# Revit family: Tyco_Fireclass_Mid Tier-I_Control and Indicating Panels - FC500______
name_source: partatom
category: Generic Models
revit_build: Autodesk Revit 2016 (Build: 20150714_1515(x64)
units: mm (PartAtom-declared; Revit-internal decimal feet)

## family parameters
Always vertical = Yes
Can host rebar = No
Cut with Voids When Loaded = No
Host = Wall
Part Type = Normal
Room Calculation Point = No
Round Connector Dimension = Use Diameter
Shared = No

## types (1)
- FC500
    Asset Type = Moveable
    Brand = FireClass
    Colour = RAL 7035
    Description = Repeater for use with FC501, FC503 and FC506 panels
    Duration Unit = Year
    Finish = Fine texture, Matt
    Has Protective Earth = TRUE
    Manufacturer = Tyco Fire & Security GmbH
    Manufacturer Name = Tyco Fire & Security GmbH
    Manufacturer URL = www.fireclass.net
    Material = Mild Steel EN10130 DC01
    Material Description = FC500 FireClass Repeater
    Model = FC500
    Model Number = FC500
    NBS Description = Fire detection and alarm control and indicating equipment (CIE)
    Name = FC500
    Nominal Frequency Range = 50/60 Hz
    Nominal Height = 234 mm  [stored 0.767717 ft]
    Nominal Length = 55.7 mm  [stored 0.182743 ft]
    Nominal Voltage = 19 Vdc - 30 Vdc
    Nominal Width = 345 mm  [stored 1.13189 ft]
    Operation Temperature Range = -5 °C to +40 °C
    Product Codes = 557.200.727
    Product Information = www.fireclass.net
    Product Specification = FireClass Repeater for use with FC501, FC503 and FC506 panels
    Relative Humidity = up to 95% RH continuous (non-condensing)
    Shape = Rectangle
    Storage Temperature = -40 °C to +80 °C
    URL = www.fireclass.net
    Usage Current = 130 mA (dc)
    Version = 1
    Warranty Description = The 36 month warranty is applicable from the date of manufacture.
    Warranty Duration Parts = 3 years
    Warranty Duration Unit = Year
    WarrantyDurationLabor = 3 years
    Weight = 2.7 Kg

note: [stored X ft] marks values corroborated as IEEE doubles in the binary element streams (Revit-internal decimal feet)

## geometry (parser evidence)
native form markers: Sweep x5
no freeform markers — native parametric forms only
